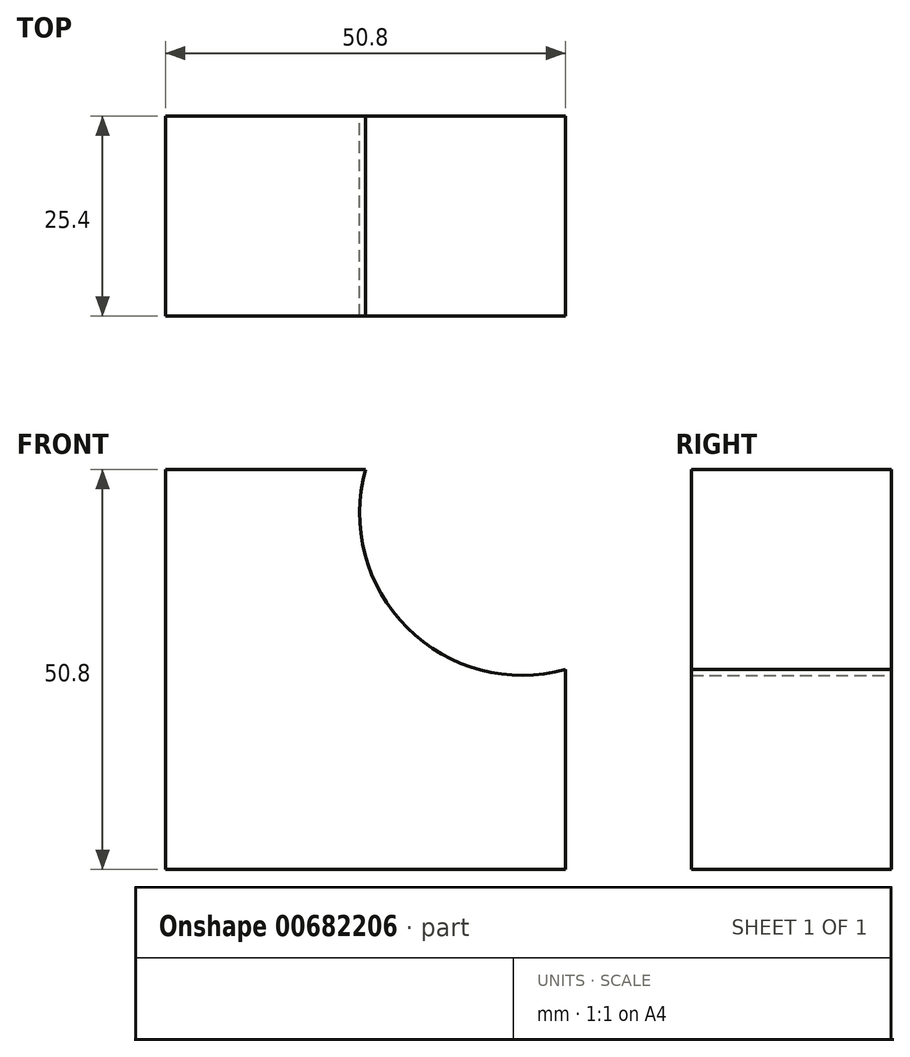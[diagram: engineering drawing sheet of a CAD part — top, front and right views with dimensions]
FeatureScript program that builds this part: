
annotation { "Feature Type Name" : "Feature", "Feature Type Description" : "" }
export const myFeature = defineFeature(function(context is Context, id is Id, definition is map)
    precondition{}
    {
        {
            var Q0;
            Q0=qCreatedBy(makeId("Front.planeOp"),FACE);
            var sketch = newSketch(context, id + "F0", { "sketchPlane" : qUnion([Q0])});
            skLineSegment(sketch, "E0", {"start": v(0, 0) * mm, "end": v(-50.8, 0) * mm});
            skLineSegment(sketch, "E1", {"start": v(-50.8, 0) * mm, "end": v(-50.8, 50.8) * mm});
            skLineSegment(sketch, "E2", {"start": v(-50.8, 50.8) * mm, "end": v(-25.4, 50.8) * mm});
            skLineSegment(sketch, "E3", {"start": v(0, 0) * mm, "end": v(0, 25.4) * mm});
            skArc(sketch, "E4", {"start": v(-25.4, 50.8) * mm, "mid": v(-20.1, 30.7) * mm, "end": v(0, 25.4) * mm});
            skSolve(sketch);
        }
        {
            var Q0;
            Q0 = qSketchRegion(id + "F0", true);
            extrude(context, id + "F1", {"entities" : qUnion([Q0]), "depth" : 25.4 * mm, "offsetDistance" : 25.4 * mm});
        }
    });
